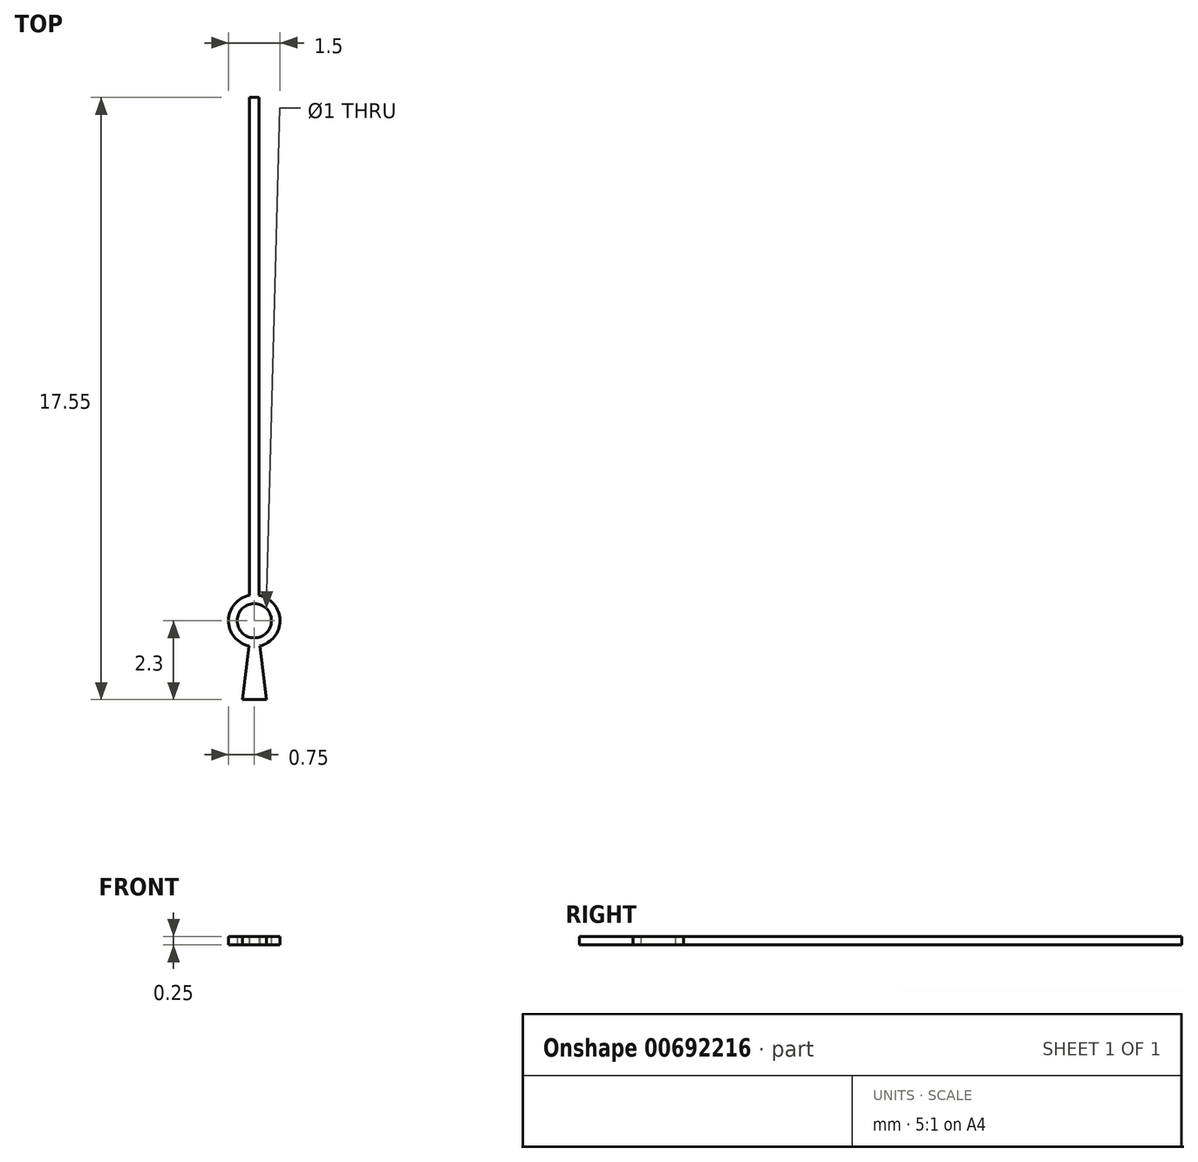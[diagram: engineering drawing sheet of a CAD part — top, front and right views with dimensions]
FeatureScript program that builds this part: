
annotation { "Feature Type Name" : "Feature", "Feature Type Description" : "" }
export const myFeature = defineFeature(function(context is Context, id is Id, definition is map)
    precondition{}
    {
        {
            var Q0;
            Q0=qCreatedBy(makeId("Top.planeOp"),FACE);
            var sketch = newSketch(context, id + "F0", { "sketchPlane" : qUnion([Q0])});
            skCircle(sketch, "E0", {"center": v(0, 0) * mm, "radius": 0.5 * mm});
            skArc(sketch, "E1", {"start": v(0.16, -0.73) * mm, "mid": v(0.75, 0) * mm, "end": v(0.14, 0.74) * mm});
            skLineSegment(sketch, "E2", {"start": v(-0.14, 0.74) * mm, "end": v(-0.14, 15.25) * mm});
            skLineSegment(sketch, "E3", {"start": v(-0.14, 15.25) * mm, "end": v(0, 15.25) * mm});
            skLineSegment(sketch, "E4", {"start": v(-0.16, -0.73) * mm, "end": v(-0.35, -2.3) * mm});
            skLineSegment(sketch, "E5", {"start": v(-0.35, -2.3) * mm, "end": v(0, -2.3) * mm});
            skLineSegment(sketch, "E6.MirrorCS", {"start": v(0.14, 15.25) * mm, "end": v(0, 15.25) * mm});
            skLineSegment(sketch, "E7.MirrorCS", {"start": v(0.14, 0.74) * mm, "end": v(0.14, 15.25) * mm});
            skLineSegment(sketch, "E8.MirrorCS", {"start": v(0.35, -2.3) * mm, "end": v(0, -2.3) * mm});
            skLineSegment(sketch, "E9.MirrorCS", {"start": v(0.16, -0.73) * mm, "end": v(0.35, -2.3) * mm});
            skArc(sketch, "E10.trimOffspring", {"start": v(-0.14, 0.74) * mm, "mid": v(-0.75, 0) * mm, "end": v(-0.16, -0.73) * mm});
            skSolve(sketch);
        }
        {
            var Q0;
            Q0 = qSketchRegion(id + "F0", true);
            extrude(context, id + "F1", {"entities" : qUnion([Q0]), "depth" : 0.25 * mm, "offsetDistance" : 25 * mm});
        }
    });
